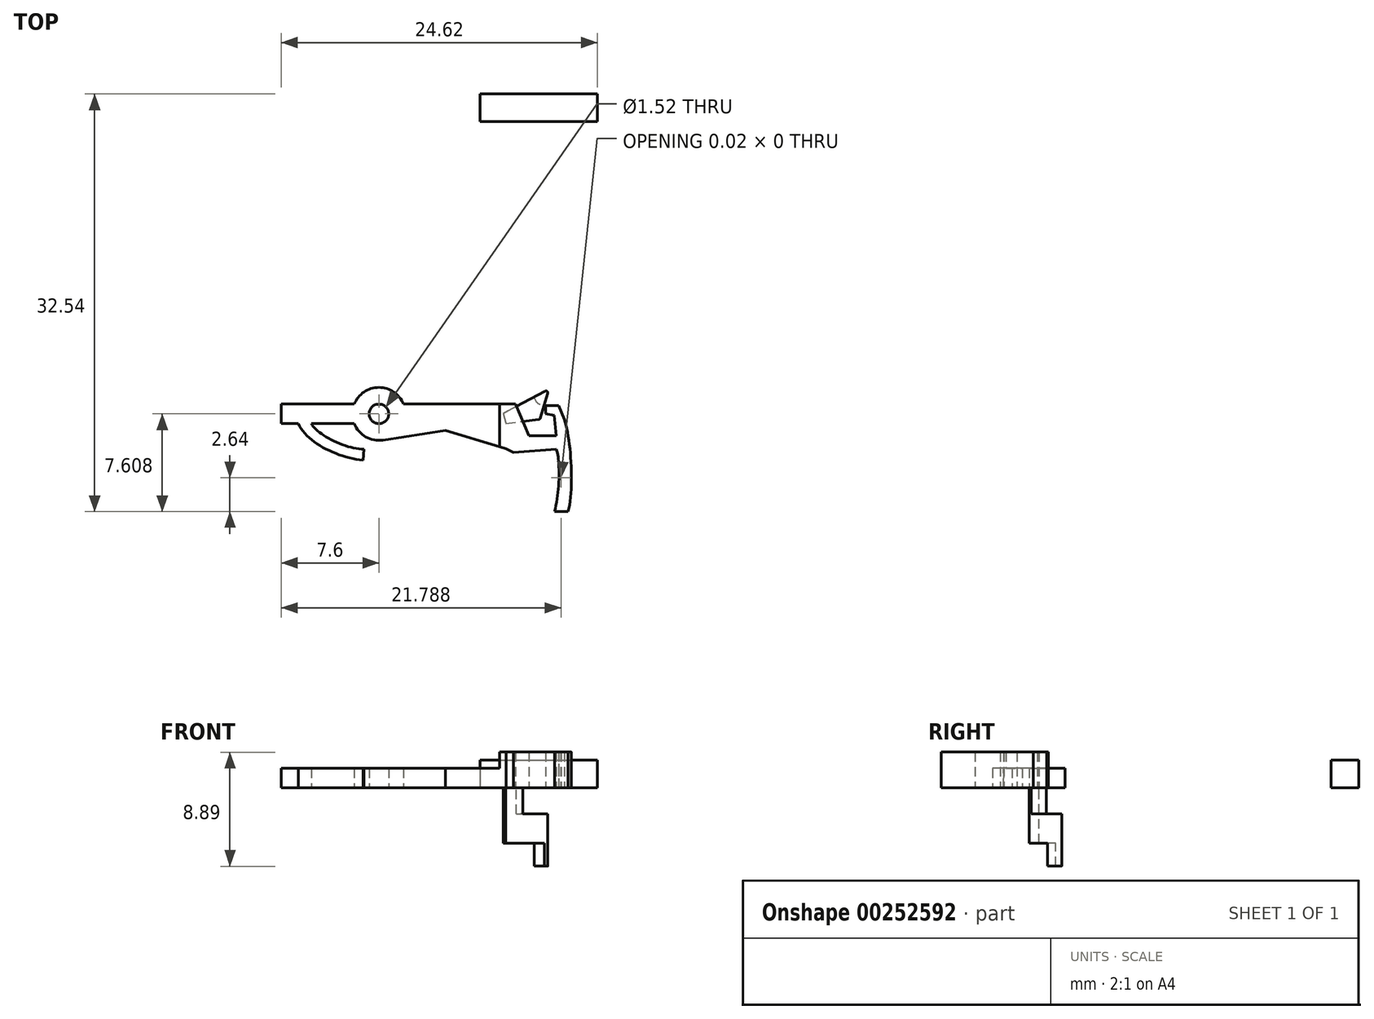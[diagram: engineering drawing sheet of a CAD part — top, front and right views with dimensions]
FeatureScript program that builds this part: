
annotation { "Feature Type Name" : "Feature", "Feature Type Description" : "" }
export const myFeature = defineFeature(function(context is Context, id is Id, definition is map)
    precondition{}
    {
        {
            var Q0;
            Q0=qCreatedBy(makeId("Top.planeOp"),FACE);
            var sketch = newSketch(context, id + "F0", { "sketchPlane" : qUnion([Q0])});
            skLineSegment(sketch, "E0.bottom", {"start": v(-52.9, -0.34) * mm, "end": v(-51.58, -0.34) * mm});
            skLineSegment(sketch, "E0.top", {"start": v(-52.9, 1.18) * mm, "end": v(-47.23, 1.18) * mm});
            skLineSegment(sketch, "E0.left", {"start": v(-52.9, -0.34) * mm, "end": v(-52.9, 1.18) * mm});
            skArc(sketch, "E1", {"start": v(-47.23, -0.34) * mm, "mid": v(-46.33, -1.38) * mm, "end": v(-44.99, -1.62) * mm});
            skCircle(sketch, "E2", {"center": v(-45.3, 0.42) * mm, "radius": 0.76 * mm});
            skLineSegment(sketch, "E3.bottom", {"start": v(-43.4, 1.18) * mm, "end": v(-34.66, 1.18) * mm});
            skFitSpline(sketch, "E4", {"points": [v(-51.58, -0.34) * mm, v(-46.55, -3.19) * mm], "startDerivative": vector(2.16, -4.51) * mm, "endDerivative": vector(6, -0.6) * mm});
            skFitSpline(sketch, "E5", {"points": [v(-50.57, -0.34) * mm, v(-46.47, -2.32) * mm], "startDerivative": vector(1.14, -2.36) * mm, "endDerivative": vector(4.38, 0.13) * mm});
            skLineSegment(sketch, "E6", {"start": v(-46.47, -2.32) * mm, "end": v(-46.55, -3.19) * mm});
            skArc(sketch, "E7.trimOffspring", {"start": v(-43.4, 1.18) * mm, "mid": v(-45.3, 2.48) * mm, "end": v(-47.23, 1.18) * mm});
            skLineSegment(sketch, "E8", {"start": v(-47.23, -0.34) * mm, "end": v(-47.07, -0.34) * mm});
            skLineSegment(sketch, "E9", {"start": v(-34.66, 1.18) * mm, "end": v(-33.62, -1.27) * mm});
            skLineSegment(sketch, "E10", {"start": v(-33.62, -1.27) * mm, "end": v(-31.48, -1.27) * mm});
            skLineSegment(sketch, "E11", {"start": v(-31.48, -1.27) * mm, "end": v(-31.66, 0.32) * mm});
            skLineSegment(sketch, "E12", {"start": v(-31.66, 0.32) * mm, "end": v(-32.3, 0.43) * mm});
            skLineSegment(sketch, "E13", {"start": v(-32.3, 0.43) * mm, "end": v(-32.3, 1.05) * mm});
            skFitSpline(sketch, "E14", {"points": [v(-30.65, -1.27) * mm, v(-31.13, -4.55) * mm, v(-31.11, -4.55) * mm], "startDerivative": vector(-0.98, -2.93) * mm, "endDerivative": vector(0.26, 0.1) * mm});
            skLineSegment(sketch, "E15", {"start": v(-32.3, 1.05) * mm, "end": v(-31.29, 1.05) * mm});
            skLineSegment(sketch, "E16", {"start": v(-31.29, 1.05) * mm, "end": v(-30.86, 0) * mm});
            skLineSegment(sketch, "E17", {"start": v(-31.11, -4.55) * mm, "end": v(-31.13, -4.55) * mm});
            skLineSegment(sketch, "E18", {"start": v(-31.48, -2.33) * mm, "end": v(-34.83, -2.59) * mm});
            skLineSegment(sketch, "E19", {"start": v(-34.83, -2.59) * mm, "end": v(-35.38, -2.3) * mm});
            skLineSegment(sketch, "E20", {"start": v(-35.38, -2.3) * mm, "end": v(-40.12, -0.85) * mm});
            skLineSegment(sketch, "E21", {"start": v(-40.12, -0.85) * mm, "end": v(-44.99, -1.62) * mm});
            skPoint(sketch, "E3.right.end.orphan", {"position": v(59.55, -0.34) * mm});
            skLineSegment(sketch, "E22.trimOffspring", {"start": v(-50.57, -0.34) * mm, "end": v(-47.07, -0.34) * mm});
            skLineSegment(sketch, "E23", {"start": v(-35.41, -0.32) * mm, "end": v(-32.87, -0.01) * mm});
            skLineSegment(sketch, "E24", {"start": v(-32.72, 0.11) * mm, "end": v(-32.15, 2.02) * mm});
            skLineSegment(sketch, "E25", {"start": v(-32.37, 2.2) * mm, "end": v(-35.63, 0.44) * mm});
            skLineSegment(sketch, "E26", {"start": v(-35.63, 0.44) * mm, "end": v(-35.41, -0.32) * mm});
            skPoint(sketch, "E27.visualSharp", {"position": v(-32.05, 2.36) * mm});
            skArc(sketch, "E27.filletArc", {"start": v(-32.15, 2.02) * mm, "mid": v(-32.2, 2.18) * mm, "end": v(-32.37, 2.2) * mm});
            skPoint(sketch, "E28.visualSharp", {"position": v(-32.75, 0) * mm});
            skArc(sketch, "E28.filletArc", {"start": v(-32.87, -0.01) * mm, "mid": v(-32.77, 0.03) * mm, "end": v(-32.72, 0.11) * mm});
            skCircle(sketch, "E29", {"center": v(-32.46, 1.86) * mm, "radius": 0.76 * mm});
            skPoint(sketch, "E30.orphan", {"position": v(-139.8, -1.37) * mm});
            skLineSegment(sketch, "E31", {"start": v(-35.9, 1.18) * mm, "end": v(-35.9, -2.15) * mm});
            skFitSpline(sketch, "E32", {"points": [v(-30.86, 0) * mm, v(-30.56, -7.19) * mm], "startDerivative": vector(1.6, -4.83) * mm, "endDerivative": vector(-1.44, -5.53) * mm});
            skLineSegment(sketch, "E33", {"start": v(-30.56, -7.19) * mm, "end": v(-31.63, -7.19) * mm});
            skFitSpline(sketch, "E34", {"points": [v(-31.63, -7.19) * mm, v(-31.48, -2.33) * mm], "startDerivative": vector(1.56, 5.29) * mm, "endDerivative": vector(-0.7, 1.51) * mm});
            skSolve(sketch);
        }
        {
            var Q0;
            Q0=makeQuery(id+"F0.imprint","IMPRINT",FACE,{"disambiguationData":[TD([[makeQuery(id+"F0.imprint","IMPRINT",EDGE,{"derivedFrom":sQuery(id+"F0.wireOp",EDGE,"E0.bottom")}),1.0]])]});
            extrude(context, id + "F1", {"entities" : qUnion([Q0]), "depth" : 1.52 * mm});
        }
        {
            var Q0;
            {var subQ5=sQuery(id+"F0.wireOp",EDGE,"E26");Q0=makeQuery(id+"F0.imprint","IMPRINT",FACE,{"disambiguationData":[TD([[makeQuery(id+"F0.imprint","IMPRINT",EDGE,{"derivedFrom":subQ5}),1.0]])]});}
            var Q1;
            {var subQ0=sQuery(id+"F0.wireOp",EDGE,"E10");Q1=makeQuery(id+"F0.imprint","IMPRINT",FACE,{"disambiguationData":[TD([[makeQuery(id+"F0.imprint","IMPRINT",EDGE,{"derivedFrom":subQ0}),-1.0]])]});}
            extrude(context, id + "F2", {"entities" : qUnion([Q0, Q1]), "operationType" : NewBodyOperationType.ADD, "depth" : 2.8 * mm});
        }
        {
            var Q0;
            {var subQ5=sQuery(id+"F0.wireOp",EDGE,"E26");Q0=makeQuery(id+"F0.imprint","IMPRINT",FACE,{"disambiguationData":[TD([[makeQuery(id+"F0.imprint","IMPRINT",EDGE,{"derivedFrom":subQ5}),1.0]])]});}
            var Q1;
            {var subQ5=sQuery(id+"F0.wireOp",EDGE,"E28.filletArc");Q1=makeQuery(id+"F0.imprint","IMPRINT",FACE,{"disambiguationData":[TD([[makeQuery(id+"F0.imprint","IMPRINT",EDGE,{"derivedFrom":subQ5}),1.0]])]});}
            var Q2;
            {var subQ0=sQuery(id+"F0.wireOp",EDGE,"E29");var subQ1=sQuery(id+"F0.wireOp",EDGE,"E24");var subQ2=makeQuery(id+"F0.imprint","INTERSECT",VERTEX,{"disambiguationData":[OD(0.0)],"derivedFrom":[subQ1,subQ0]});Q2=makeQuery(id+"F0.imprint","IMPRINT",FACE,{"disambiguationData":[TD([[makeQuery(id+"F0.imprint","IMPRINT",EDGE,{"disambiguationData":[TD([[subQ2,-1.0]])],"derivedFrom":subQ1}),1.0]])]});}
            extrude(context, id + "F3", {"entities" : qUnion([Q0, Q1, Q2]), "operationType" : NewBodyOperationType.ADD, "oppositeDirection" : true, "depth" : 2.03 * mm});
        }
        {
            var Q0;
            Q0=makeQuery(id+"F3.opExtrude","CAP_FACE",FACE,{"disambiguationData":[OSD([sQuery(id+"F0.wireOp",EDGE,"E23"),sQuery(id+"F0.wireOp",EDGE,"E24"),sQuery(id+"F0.wireOp",EDGE,"E25"),sQuery(id+"F0.wireOp",EDGE,"E26"),sQuery(id+"F0.wireOp",EDGE,"E28.filletArc"),sQuery(id+"F0.wireOp",EDGE,"E29")])],"isStart":false});
            extrude(context, id + "F4", {"entities" : qUnion([Q0]), "operationType" : NewBodyOperationType.ADD, "depth" : 2.3 * mm});
        }
        {
            var Q0;
            {var subQ5=sQuery(id+"F0.wireOp",EDGE,"E28.filletArc");Q0=makeQuery(id+"F0.imprint","IMPRINT",FACE,{"disambiguationData":[TD([[makeQuery(id+"F0.imprint","IMPRINT",EDGE,{"derivedFrom":subQ5}),1.0]])]});}
            var Q1;
            {var subQ0=sQuery(id+"F0.wireOp",EDGE,"E29");var subQ1=sQuery(id+"F0.wireOp",EDGE,"E24");var subQ2=makeQuery(id+"F0.imprint","INTERSECT",VERTEX,{"disambiguationData":[OD(0.0)],"derivedFrom":[subQ1,subQ0]});Q1=makeQuery(id+"F0.imprint","IMPRINT",FACE,{"disambiguationData":[TD([[makeQuery(id+"F0.imprint","IMPRINT",EDGE,{"disambiguationData":[TD([[subQ2,-1.0]])],"derivedFrom":subQ1}),1.0]])]});}
            extrude(context, id + "F5", {"entities" : qUnion([Q0, Q1]), "operationType" : NewBodyOperationType.REMOVE, "oppositeDirection" : true, "depth" : 2.03 * mm});
        }
        {
            var Q0;
            {var subQ0=sQuery(id+"F0.wireOp",EDGE,"E29");var subQ1=sQuery(id+"F0.wireOp",EDGE,"E24");var subQ2=makeQuery(id+"F0.imprint","INTERSECT",VERTEX,{"disambiguationData":[OD(0.0)],"derivedFrom":[subQ1,subQ0]});Q0=makeQuery(id+"F0.imprint","IMPRINT",FACE,{"disambiguationData":[TD([[makeQuery(id+"F0.imprint","IMPRINT",EDGE,{"disambiguationData":[TD([[subQ2,-1.0]])],"derivedFrom":subQ1}),1.0]])]});}
            extrude(context, id + "F6", {"entities" : qUnion([Q0]), "operationType" : NewBodyOperationType.ADD, "oppositeDirection" : true, "depth" : 6.1 * mm});
        }
        {
            var Q0;
            {var subQ0=sQuery(id+"F0.wireOp",EDGE,"E29");var subQ1=sQuery(id+"F0.wireOp",EDGE,"E24");var subQ2=makeQuery(id+"F0.imprint","INTERSECT",VERTEX,{"disambiguationData":[OD(0.0)],"derivedFrom":[subQ1,subQ0]});Q0=makeQuery(id+"F0.imprint","IMPRINT",FACE,{"disambiguationData":[TD([[makeQuery(id+"F0.imprint","IMPRINT",EDGE,{"disambiguationData":[TD([[subQ2,-1.0]])],"derivedFrom":subQ1}),1.0]])]});}
            var Q1;
            Q1=makeQuery(id+"F5.boolean.opBoolean","COPY",FACE,{"derivedFrom":makeQuery(id+"F5.opExtrude","CAP_FACE",FACE,{"disambiguationData":[OSD([sQuery(id+"F0.wireOp",EDGE,"E9"),sQuery(id+"F0.wireOp",EDGE,"E23"),sQuery(id+"F0.wireOp",EDGE,"E24"),sQuery(id+"F0.wireOp",EDGE,"E25"),sQuery(id+"F0.wireOp",EDGE,"E28.filletArc"),sQuery(id+"F0.wireOp",EDGE,"E29")])],"isStart":false})});
            extrude(context, id + "F7", {"entities" : qUnion([Q0]), "operationType" : NewBodyOperationType.REMOVE, "endBound" : BoundingType.UP_TO_SURFACE, "oppositeDirection" : true, "endBoundEntityFace" : qUnion([Q1]), "depth" : 25.4 * mm});
        }
        {
            var Q0;
            Q0=qCreatedBy(makeId("Top.planeOp"),FACE);
            var sketch = newSketch(context, id + "F8", { "sketchPlane" : qUnion([Q0])});
            skLineSegment(sketch, "E35.bottom", {"start": v(-37.43, 25.35) * mm, "end": v(-28.29, 25.35) * mm});
            skLineSegment(sketch, "E35.top", {"start": v(-37.43, 23.19) * mm, "end": v(-28.29, 23.19) * mm});
            skLineSegment(sketch, "E35.left", {"start": v(-37.43, 25.35) * mm, "end": v(-37.43, 23.19) * mm});
            skLineSegment(sketch, "E35.right", {"start": v(-28.29, 25.35) * mm, "end": v(-28.29, 23.19) * mm});
            skSolve(sketch);
        }
        {
            var Q0;
            Q0=makeQuery(id+"F8.imprint","IMPRINT",FACE,{"disambiguationData":[TD([[makeQuery(id+"F8.imprint","IMPRINT",EDGE,{"derivedFrom":sQuery(id+"F8.wireOp",EDGE,"E35.bottom")}),-1.0]])]});
            extrude(context, id + "F9", {"entities" : qUnion([Q0]), "depth" : 2.16 * mm});
        }
    });
